# Revit family: Power-ModularDevices-GEWISS-90AM-CONTACTORS_63A
name_source: partatom
category: Apparecchi elettrici
revit_build: Autodesk Revit 2016 (Build: 20161004_0715(x64)
units: mm (PartAtom-declared; Revit-internal decimal feet)

## family parameters
Condiviso = No
Host = Superficie
Mantenere orientamento annotazione = Sì
Numero OmniClass = 23.80.30.00
Punto di calcolo locali = Sì
Quota connettore circolare = Usa diametro
Taglio con vuoti quando caricato = No
Tipo di parte = Normale
Titolo OmniClass = Distribution Devices

## types (5) — shared parameters
A = 54 mm  [stored 0.177165 ft]
B = 85 mm  [stored 0.278871 ft]
C = 65 mm  [stored 0.213255 ft]
Catalogue = POWER
Catalogue Range = 90 AM
D = 45 mm  [stored 0.147638 ft]
Electrocod = 1712
Fin_contattore = <Per categoria>
IDF = 21306ecf-3ec0-4b82-b9e7-bfcac6a47091
IDT = c63d6545-c37d-42b5-b4d1-4d04d153b494
Immagine tipo = GWD6735.jpg
No. Chorus modules = 3
Numero poli = 1
Potenza in Watt = 0 V
Produttore = GEWISS S.p.A.
Prospetto di default = 1219 mm
Rated current (AC-1/AC-7a) = 63 A - CTR63
TEXT LABEL = A
Technical sheet = https://www.gewiss.com
URL = https://www.gewiss.com
Version file RFA = 18.0

## per-type parameters (varying)
| type | Control coil voltage (V) | Descrizione | EAN code | Modello |
| GWD6734 - CONTACTOR 63A 4NO 230V 3M | 230Vac - 220Vdc | CONTACTOR 63A 4NO 230V 3M | 8011564809666 | GWD6734 |
| GWD6732 - CONTACTOR 63A 3NO 230V 3M | 230Vac - 220Vdc | CONTACTOR 63A 3NO 230V 3M | 8011564809642 | GWD6732 |
| GWD6735 - CONTACTOR 63A 3NO+1NC 230V 3M | 230Vac - 220Vdc | CONTACTOR 63A 3NO+1NC 230V 3M | 8011564809673 | GWD6735 |
| GWD6733 - CONTACTOR 63A 4NO 24V 3M | 24Vac/dc | CONTACTOR 63A 4NO 24V 3M | 8011564809659 | GWD6733 |
| GWD6731 - CONTACTOR 63A 2NO 230V 3M | 230Vac - 220Vdc | CONTACTOR 63A 2NO 230V 3M | 8011564809635 | GWD6731 |

note: [stored X ft] marks values corroborated as IEEE doubles in the binary element streams (Revit-internal decimal feet)
